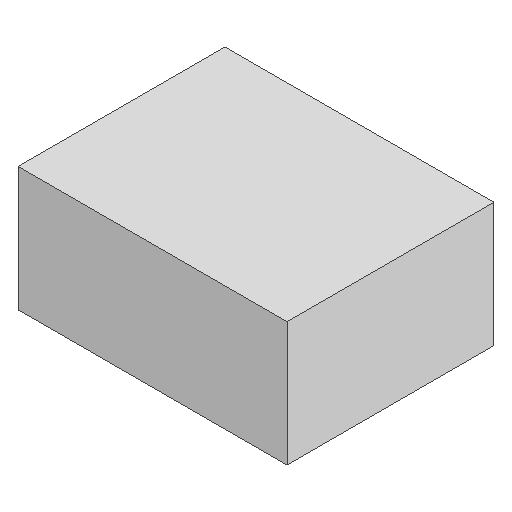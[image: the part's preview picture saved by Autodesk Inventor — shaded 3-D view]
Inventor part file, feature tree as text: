
AUTODESK INVENTOR PART (.ipt)
format: ipt  version: 2025.2 (Build 292293000, 293)  size: 105,472 bytes
history: native  units: mm
features: extrude x2, sketch x2
ambient origin geometry x8: Origin, YZ Plane, XZ Plane, XY Plane, X Axis, Y Axis, Z Axis, Center Point
bodies: Solid1 (feature_tree)
feature tree (4):
  extrude  "Extrusion1"  Depth=6.0mm
  extrude  "Extrusion2"  Depth=11.5mm
  sketch  "Sketch1"  dims[d0=13.0mm d1=6.0mm]
  sketch  "Sketch2"  dims[d2=10.0mm d3=0.0mm d4=11.5mm d5=0.2mm d6=0.2mm d7=3.0mm d8=1.0mm d9=9.8mm d10=0.0mm]
